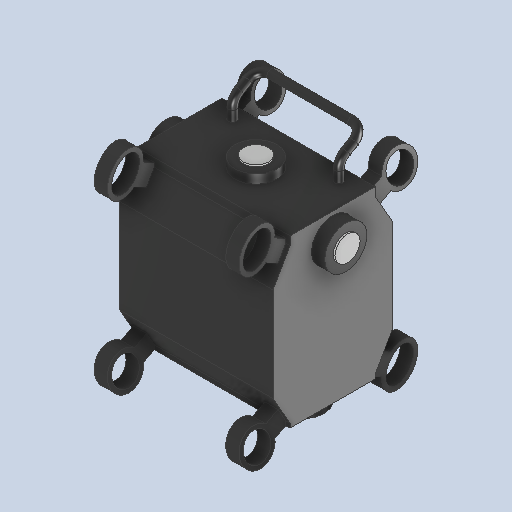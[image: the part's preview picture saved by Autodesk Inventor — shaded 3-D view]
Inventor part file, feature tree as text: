
AUTODESK INVENTOR PART (.ipt)
format: ipt  version: 2024.2 (Build 282272000, 272)  size: 1,047,040 bytes
history: native  units: mm
features: other x34, delete_face x7, move_body x5, direct_edit x1, extrude x1, sketch x1
ambient origin geometry x8: Origin, YZ Plane, XZ Plane, XY Plane, X Axis, Y Axis, Z Axis, Center Point
bodies: Solid1 (feature_tree)
feature tree (49):
  other  "TorsoBlock.iam"
  other  "TorsoUnit.iam:1::CrossRollerBearingUnit.iam:1::CrossRollerBearingOuterFlange.ipt:1"
  other  "TorsoUnit.iam:1::CrossRollerBearingUnit.iam:1::CrossRollerBearingOuterSupportStand.ipt:1"
  other  "TorsoUnit.iam:1::CrossRollerBearingUnit.iam:1::CrossRollerBearingInnerSupportStand.ipt:1"
  other  "TorsoUnit.iam:1::UHFNB125.ipt:1"
  other  "TorsoUnit.iam:1::CrossRollerBearingUnit.iam:2::CrossRollerBearingOuterFlange.ipt:1"
  other  "TorsoUnit.iam:1::CrossRollerBearingUnit.iam:2::CrossRollerBearingOuterSupportStand.ipt:1"
  other  "TorsoUnit.iam:1::CrossRollerBearingUnit.iam:2::CrossRollerBearingInnerSupportStand.ipt:1"
  other  "TorsoUnit.iam:1::TorsoFrontCoverFrame.ipt:1"
  other  "TorsoUnit.iam:1::CrossRollerBearingUnit.iam:3::CrossRollerBearingOuterFlange.ipt:1"
  other  "TorsoUnit.iam:1::CrossRollerBearingUnit.iam:3::CrossRollerBearingOuterSupportStand.ipt:1"
  other  "TorsoUnit.iam:1::CrossRollerBearingUnit.iam:3::CrossRollerBearingInnerSupportStand.ipt:1"
  other  "TorsoUnit.iam:1::TorsoFrontBumper.ipt:1"
  other  "TorsoUnit.iam:1::TorsoFrontBumper.ipt:2"
  other  "TorsoUnit.iam:1::TorsoFrontBumper.ipt:3"
  other  "TorsoUnit.iam:1::TorsoFrontBumper.ipt:4"
  other  "TorsoUnit.iam:1::TorsoUpperFrame.ipt:2"
  other  "TorsoUnit.iam:1::TorsoBackBumper.ipt:1"
  other  "TorsoUnit.iam:1::TorsoBackBumper.ipt:2"
  other  "TorsoUnit.iam:1::TorsoBackBumper.ipt:3"
  other  "TorsoUnit.iam:1::TorsoBackBumper.ipt:4"
  other  "TorsoUnit.iam:1::TorsoSideFrame_.ipt:1"
  other  "TorsoUnit.iam:1::TorsoSideFrame_.ipt:2"
  other  "TorsoPelvisUnit.iam:1::TorsoPelvisLowerFrame.ipt:1"
  other  "TorsoPelvisUnit.iam:1::CrossRollerBearingUnit.iam:1::CrossRollerBearingOuterFlange.ipt:1"
  other  "TorsoPelvisUnit.iam:1::CrossRollerBearingUnit.iam:1::CrossRollerBearingOuterSupportStand.ipt:1"
  other  "TorsoPelvisUnit.iam:1::CrossRollerBearingUnit.iam:1::CrossRollerBearingInnerSupportStand.ipt:1"
  other  "TorsoPelvisUnit.iam:1::CrossRollerBearingUnit.iam:2::CrossRollerBearingOuterFlange.ipt:1"
  other  "TorsoPelvisUnit.iam:1::CrossRollerBearingUnit.iam:2::CrossRollerBearingOuterSupportStand.ipt:1"
  other  "TorsoPelvisUnit.iam:1::CrossRollerBearingUnit.iam:2::CrossRollerBearingInnerSupportStand.ipt:1"
  other  "TorsoElectronicBoxUnit.iam:1::TorsoElectronicBoxBackFrame.ipt:1"
  other  "TorsoBlock.iam_Bodies"
  other  "TorsoUnit.iam:1::UZB.ipt:1"
  other  "TorsoUnit.iam:1::UZB.ipt:2"
  delete_face  "Delete Face1"
  delete_face  "Delete Face2"
  delete_face  "Delete Face3"
  direct_edit  "Direct Edit2"
  delete_face  "Delete Face4"
  delete_face  "Delete Face5"
  delete_face  "Delete Face6"
  delete_face  "Delete Face7"
  extrude  "Extrusion1"  Depth=5.5mm TaperAngle=0.0deg
  sketch  "Sketch1"  dims[d0=10.0mm d7=0.0mm d8=0.0mm d9=5.5mm d10=0.0mm d11=0.0mm d12=5.5mm d13=0.0mm d14=0.0mm d15=5.5mm d16=0.0mm d17=0.0mm d18=5.5mm d19=0.0mm d20=0.0mm d21=5.5mm d22=10.0mm d23=0.0mm]
  move_body  "Move3"
  move_body  "Move4"
  move_body  "Move5"
  move_body  "Move6"
  move_body  "Move7"
